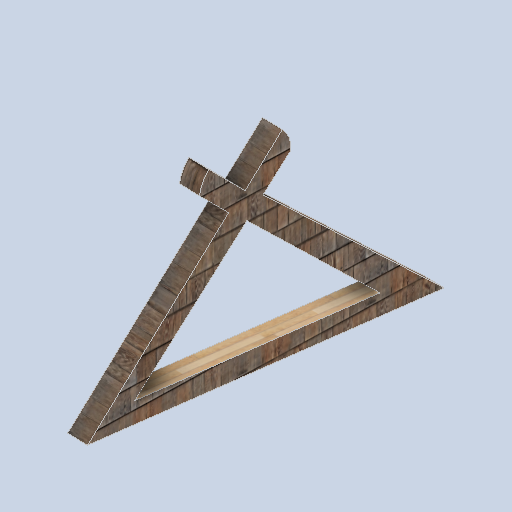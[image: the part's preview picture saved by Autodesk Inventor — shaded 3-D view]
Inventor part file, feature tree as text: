
AUTODESK INVENTOR PART (.ipt)
format: ipt  version: 2024.2 (Build 282272000, 272)  size: 233,472 bytes
history: native  units: in
note: dims shown in document units (in); Inventor stores cm internally (conversion verified against a paired STEP export)
features: sketch x10, plane x8, other x3
ambient origin geometry x8: Origin, YZ Plane, XZ Plane, XY Plane, X Axis, Y Axis, Z Axis, Center Point
bodies: Solid1 (feature_tree)
feature tree (21):
  other  "pad_outframe_02.ipt"
  other  "Solid1::pad_outframe_02.ipt"
  other  "TaggingFeature1"
  sketch  "Sketch1"  dims[d0=0.3937in]
  sketch  "Sketch2"
  sketch  "Sketch3"
  sketch  "Sketch6"
  sketch  "Sketch7"
  sketch  "Sketch8"
  sketch  "Sketch9"
  sketch  "Sketch10"
  sketch  "Sketch11"
  sketch  "Sketch12"
  plane  "Work Plane1"
  plane  "Work Plane2"
  plane  "Work Plane3"
  plane  "Work Plane4"
  plane  "Work Plane5"
  plane  "Work Plane6"
  plane  "Work Plane7"
  plane  "Work Plane8"
